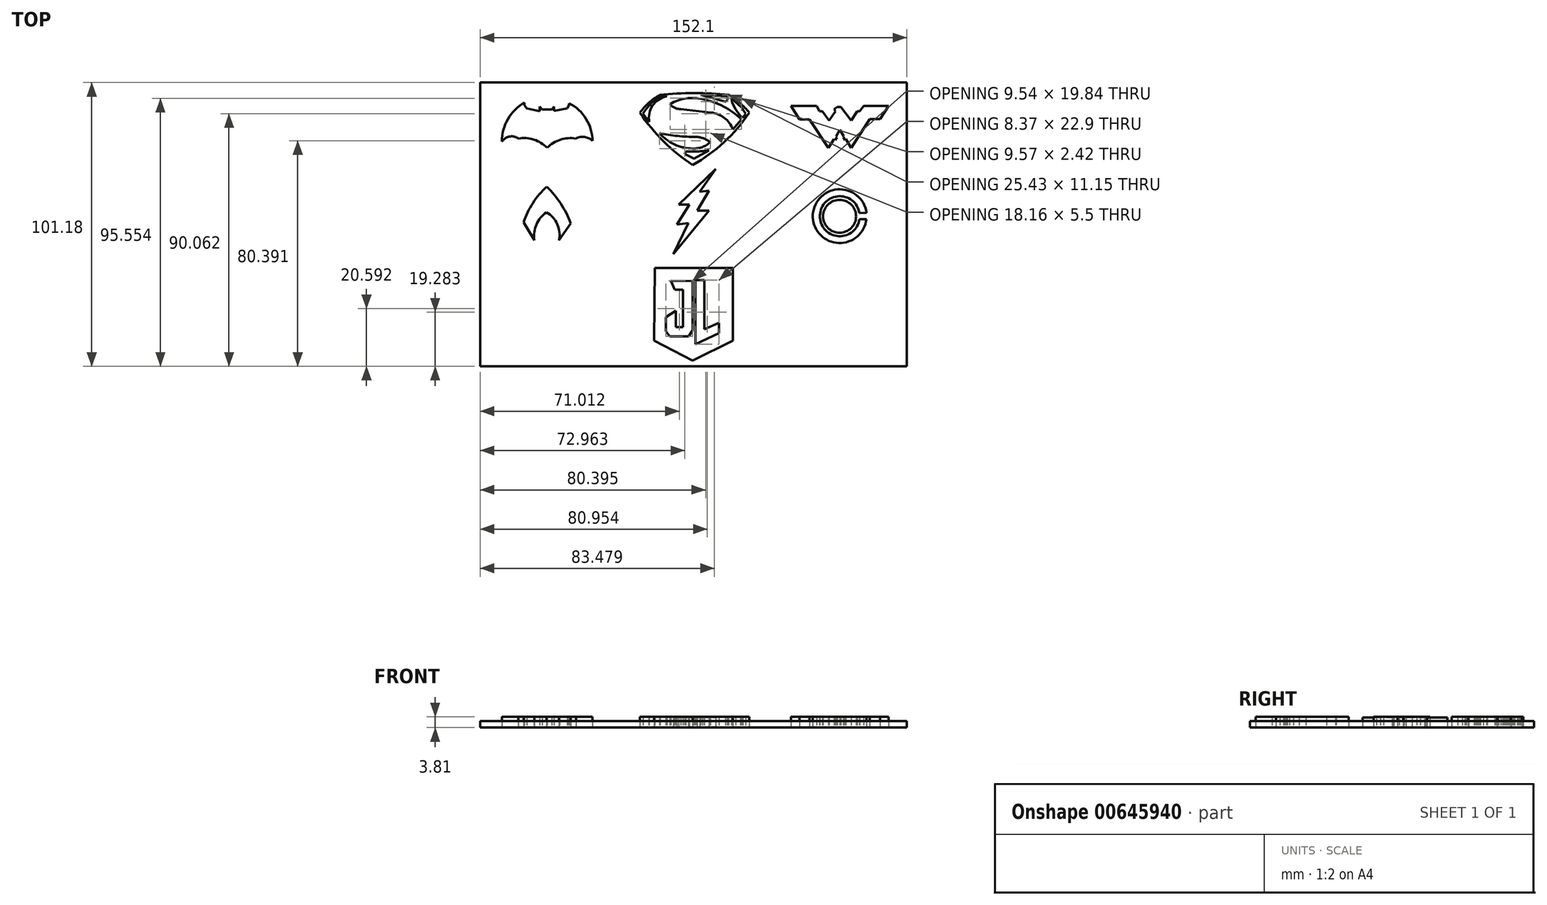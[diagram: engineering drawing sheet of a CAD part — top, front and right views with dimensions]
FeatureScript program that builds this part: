
annotation { "Feature Type Name" : "Feature", "Feature Type Description" : "" }
export const myFeature = defineFeature(function(context is Context, id is Id, definition is map)
    precondition{}
    {
        {
            var Q0;
            Q0=qCreatedBy(makeId("Top.planeOp"),FACE);
            var sketch = newSketch(context, id + "F0", { "sketchPlane" : qUnion([Q0])});
            skLineSegment(sketch, "E0.bottom", {"start": v(-75.78, 55.4) * mm, "end": v(76.32, 55.4) * mm});
            skLineSegment(sketch, "E0.top", {"start": v(-75.78, -45.78) * mm, "end": v(76.32, -45.78) * mm});
            skLineSegment(sketch, "E0.left", {"start": v(-75.78, 55.4) * mm, "end": v(-75.78, -45.78) * mm});
            skLineSegment(sketch, "E0.right", {"start": v(76.32, 55.4) * mm, "end": v(76.32, -45.78) * mm});
            skSolve(sketch);
        }
        {
            var Q0;
            Q0=makeQuery(id+"F0.imprint","IMPRINT",FACE,{"disambiguationData":[TD([[makeQuery(id+"F0.imprint","IMPRINT",EDGE,{"derivedFrom":sQuery(id+"F0.wireOp",EDGE,"E0.bottom")}),-1.0]])]});
            var sketch = newSketch(context, id + "F1", { "sketchPlane" : qUnion([Q0])});
            skLineSegment(sketch, "E1", {"start": v(-59.95, 48.2) * mm, "end": v(-59.95, 47.3) * mm});
            skLineSegment(sketch, "E2", {"start": v(-59.95, 47.3) * mm, "end": v(-59.08, 46.2) * mm});
            skLineSegment(sketch, "E3", {"start": v(-59.08, 46.2) * mm, "end": v(-54.48, 45.15) * mm});
            skLineSegment(sketch, "E4", {"start": v(-54.48, 45.15) * mm, "end": v(-54.48, 46.8) * mm});
            skLineSegment(sketch, "E5", {"start": v(-54.48, 46.8) * mm, "end": v(-53.64, 45.8) * mm});
            skLineSegment(sketch, "E6", {"start": v(-53.64, 45.8) * mm, "end": v(-50.18, 45.8) * mm});
            skLineSegment(sketch, "E7", {"start": v(-50.18, 45.8) * mm, "end": v(-49.45, 46.84) * mm});
            skLineSegment(sketch, "E8", {"start": v(-49.45, 46.84) * mm, "end": v(-49.45, 45.24) * mm});
            skLineSegment(sketch, "E9", {"start": v(-49.45, 45.24) * mm, "end": v(-44.72, 46.23) * mm});
            skLineSegment(sketch, "E10", {"start": v(-44.72, 46.23) * mm, "end": v(-44.22, 47.1) * mm});
            skLineSegment(sketch, "E11", {"start": v(-44.22, 47.1) * mm, "end": v(-43.96, 47.97) * mm});
            skArc(sketch, "E12", {"start": v(-35.7, 34.6) * mm, "mid": v(-38, 42.42) * mm, "end": v(-43.96, 47.97) * mm});
            skArc(sketch, "E13", {"start": v(-35.7, 34.6) * mm, "mid": v(-38.53, 35.98) * mm, "end": v(-41.63, 35.44) * mm});
            skArc(sketch, "E14", {"start": v(-41.63, 35.44) * mm, "mid": v(-47.16, 35.03) * mm, "end": v(-51.9, 32.16) * mm});
            skArc(sketch, "E15", {"start": v(-51.9, 32.16) * mm, "mid": v(-56.6, 35.05) * mm, "end": v(-62.1, 35.44) * mm});
            skArc(sketch, "E16", {"start": v(-62.1, 35.44) * mm, "mid": v(-65.25, 36.15) * mm, "end": v(-67.94, 34.35) * mm});
            skArc(sketch, "E17", {"start": v(-59.95, 48.2) * mm, "mid": v(-65.88, 42.39) * mm, "end": v(-67.94, 34.35) * mm});
            skSolve(sketch);
        }
        {
            var Q0;
            Q0=qCreatedBy(makeId("Top.planeOp"),FACE);
            var sketch = newSketch(context, id + "F2", { "sketchPlane" : qUnion([Q0])});
            skArc(sketch, "E18", {"start": v(-52.01, 18.27) * mm, "mid": v(-56.96, 12.44) * mm, "end": v(-60.24, 5.53) * mm});
            skLineSegment(sketch, "E19", {"start": v(-60.24, 5.53) * mm, "end": v(-56.46, -0.8) * mm});
            skArc(sketch, "E20", {"start": v(-52.1, 9.15) * mm, "mid": v(-55.72, 4.8) * mm, "end": v(-56.46, -0.8) * mm});
            skArc(sketch, "E21", {"start": v(-47.66, -0.8) * mm, "mid": v(-48.28, 4.89) * mm, "end": v(-52.1, 9.15) * mm});
            skLineSegment(sketch, "E22", {"start": v(-47.66, -0.8) * mm, "end": v(-43.46, 5.2) * mm});
            skArc(sketch, "E23", {"start": v(-43.46, 5.2) * mm, "mid": v(-47, 12.21) * mm, "end": v(-52.01, 18.27) * mm});
            skSolve(sketch);
        }
        {
            var Q0;
            Q0=qCreatedBy(makeId("Top.planeOp"),FACE);
            var sketch = newSketch(context, id + "F3", { "sketchPlane" : qUnion([Q0])});
            skLineSegment(sketch, "E24", {"start": v(8.22, 24.54) * mm, "end": v(-4.99, 11.94) * mm});
            skLineSegment(sketch, "E25", {"start": v(-4.99, 11.94) * mm, "end": v(-1.2, 11.94) * mm});
            skLineSegment(sketch, "E26", {"start": v(-1.2, 11.94) * mm, "end": v(-5.65, 4.83) * mm});
            skLineSegment(sketch, "E27", {"start": v(-5.65, 4.83) * mm, "end": v(-1.62, 5.32) * mm});
            skLineSegment(sketch, "E28", {"start": v(-1.62, 5.32) * mm, "end": v(-6.88, -5.74) * mm});
            skLineSegment(sketch, "E29", {"start": v(-6.88, -5.74) * mm, "end": v(5.8, 9.8) * mm});
            skLineSegment(sketch, "E30", {"start": v(5.8, 9.8) * mm, "end": v(1.67, 9.8) * mm});
            skLineSegment(sketch, "E31", {"start": v(1.67, 9.8) * mm, "end": v(5.86, 16.8) * mm});
            skLineSegment(sketch, "E32", {"start": v(5.86, 16.8) * mm, "end": v(2.49, 16.45) * mm});
            skLineSegment(sketch, "E33", {"start": v(2.49, 16.45) * mm, "end": v(8.22, 24.54) * mm});
            skSolve(sketch);
        }
        {
            var Q0;
            Q0=qCreatedBy(makeId("Top.planeOp"),FACE);
            var sketch = newSketch(context, id + "F4", { "sketchPlane" : qUnion([Q0])});
            skCircle(sketch, "E34", {"center": v(52.34, 7.72) * mm, "radius": 5.87 * mm});
            skArc(sketch, "E35", {"start": v(61.92, 8.95) * mm, "mid": v(51.6, 17.3) * mm, "end": v(42.8, 7.35) * mm});
            skArc(sketch, "E36", {"start": v(42.8, 7.35) * mm, "mid": v(52.04, -1.8) * mm, "end": v(61.88, 6.69) * mm});
            skLineSegment(sketch, "E37", {"start": v(61.88, 6.69) * mm, "end": v(59.42, 6.69) * mm});
            skArc(sketch, "E38", {"start": v(45.35, 7.35) * mm, "mid": v(52.09, 0.62) * mm, "end": v(59.42, 6.69) * mm});
            skArc(sketch, "E39", {"start": v(59.38, 8.83) * mm, "mid": v(51.65, 14.85) * mm, "end": v(45.35, 7.35) * mm});
            skLineSegment(sketch, "E40", {"start": v(59.38, 8.83) * mm, "end": v(61.92, 8.95) * mm});
            skSolve(sketch);
        }
        {
            var Q0;
            Q0=qCreatedBy(makeId("Top.planeOp"),FACE);
            var sketch = newSketch(context, id + "F5", { "sketchPlane" : qUnion([Q0])});
            skLineSegment(sketch, "E41", {"start": v(34.98, 47.06) * mm, "end": v(44.11, 47.06) * mm});
            skLineSegment(sketch, "E42", {"start": v(44.11, 47.06) * mm, "end": v(45.16, 45.14) * mm});
            skLineSegment(sketch, "E43", {"start": v(45.16, 45.14) * mm, "end": v(46.2, 45.14) * mm});
            skLineSegment(sketch, "E44", {"start": v(46.2, 45.14) * mm, "end": v(48.6, 41.88) * mm});
            skLineSegment(sketch, "E45", {"start": v(48.6, 41.88) * mm, "end": v(50.92, 45.14) * mm});
            skLineSegment(sketch, "E46", {"start": v(50.92, 45.14) * mm, "end": v(50.4, 45.91) * mm});
            skLineSegment(sketch, "E47", {"start": v(50.4, 45.91) * mm, "end": v(51.51, 46.66) * mm});
            skLineSegment(sketch, "E48", {"start": v(51.51, 46.66) * mm, "end": v(52.85, 46.66) * mm});
            skLineSegment(sketch, "E49", {"start": v(52.85, 46.66) * mm, "end": v(56.41, 41.86) * mm});
            skLineSegment(sketch, "E50", {"start": v(56.41, 41.86) * mm, "end": v(58.66, 45.14) * mm});
            skLineSegment(sketch, "E51", {"start": v(58.66, 45.14) * mm, "end": v(59.56, 45.14) * mm});
            skLineSegment(sketch, "E52", {"start": v(59.56, 45.14) * mm, "end": v(60.9, 47.09) * mm});
            skLineSegment(sketch, "E53", {"start": v(60.9, 47.09) * mm, "end": v(69.8, 47.09) * mm});
            skLineSegment(sketch, "E54", {"start": v(69.8, 47.09) * mm, "end": v(66.82, 42.31) * mm});
            skLineSegment(sketch, "E55", {"start": v(66.82, 42.31) * mm, "end": v(63.12, 42.31) * mm});
            skLineSegment(sketch, "E56", {"start": v(63.12, 42.31) * mm, "end": v(56.45, 32.05) * mm});
            skLineSegment(sketch, "E57", {"start": v(56.45, 32.05) * mm, "end": v(54.58, 35.26) * mm});
            skLineSegment(sketch, "E58", {"start": v(54.58, 35.26) * mm, "end": v(54.3, 34.83) * mm});
            skLineSegment(sketch, "E59", {"start": v(54.3, 34.83) * mm, "end": v(53.62, 35.9) * mm});
            skLineSegment(sketch, "E60", {"start": v(53.62, 35.9) * mm, "end": v(53.81, 36.3) * mm});
            skLineSegment(sketch, "E61", {"start": v(53.81, 36.3) * mm, "end": v(52.44, 38.55) * mm});
            skLineSegment(sketch, "E62", {"start": v(52.44, 38.55) * mm, "end": v(51.1, 36.32) * mm});
            skLineSegment(sketch, "E63", {"start": v(51.1, 36.32) * mm, "end": v(51.34, 35.88) * mm});
            skLineSegment(sketch, "E64", {"start": v(51.34, 35.88) * mm, "end": v(50.7, 34.88) * mm});
            skLineSegment(sketch, "E65", {"start": v(50.7, 34.88) * mm, "end": v(50.41, 35.26) * mm});
            skLineSegment(sketch, "E66", {"start": v(50.41, 35.26) * mm, "end": v(48.36, 32.05) * mm});
            skLineSegment(sketch, "E67", {"start": v(48.36, 32.05) * mm, "end": v(41.64, 42.25) * mm});
            skLineSegment(sketch, "E68", {"start": v(41.64, 42.25) * mm, "end": v(38.09, 42.25) * mm});
            skLineSegment(sketch, "E69", {"start": v(38.09, 42.25) * mm, "end": v(34.98, 47.06) * mm});
            skSolve(sketch);
        }
        {
            var Q0;
            Q0=qCreatedBy(makeId("Top.planeOp"),FACE);
            var sketch = newSketch(context, id + "F6", { "sketchPlane" : qUnion([Q0])});
            skArc(sketch, "E70", {"start": v(-11.68, 50.98) * mm, "mid": v(-15.6, 48.22) * mm, "end": v(-18.79, 44.64) * mm});
            skArc(sketch, "E71", {"start": v(-18.79, 44.64) * mm, "mid": v(-10.36, 34.37) * mm, "end": v(0, 26.04) * mm});
            skArc(sketch, "E72", {"start": v(0, 26.04) * mm, "mid": v(11.19, 34.14) * mm, "end": v(20.15, 44.64) * mm});
            skArc(sketch, "E73", {"start": v(20.15, 44.64) * mm, "mid": v(16.76, 48.18) * mm, "end": v(12.76, 51) * mm});
            skArc(sketch, "E74", {"start": v(12.76, 51) * mm, "mid": v(0.54, 51.62) * mm, "end": v(-11.68, 50.98) * mm});
            skLineSegment(sketch, "E75", {"start": v(17.87, 42.85) * mm, "end": v(18.86, 44.22) * mm});
            skLineSegment(sketch, "E76", {"start": v(18.86, 44.22) * mm, "end": v(17.3, 46.54) * mm});
            skLineSegment(sketch, "E77", {"start": v(17.3, 46.54) * mm, "end": v(13.83, 49.72) * mm});
            skLineSegment(sketch, "E78", {"start": v(13.83, 49.72) * mm, "end": v(14.07, 48.26) * mm});
            skLineSegment(sketch, "E79", {"start": v(14.07, 48.26) * mm, "end": v(15.32, 45.81) * mm});
            skLineSegment(sketch, "E80", {"start": v(15.32, 45.81) * mm, "end": v(17.03, 43.51) * mm});
            skLineSegment(sketch, "E81", {"start": v(17.03, 43.51) * mm, "end": v(17.87, 42.85) * mm});
            skLineSegment(sketch, "E82", {"start": v(2.92, 50.98) * mm, "end": v(12.25, 50.53) * mm});
            skArc(sketch, "E83", {"start": v(11.63, 48.56) * mm, "mid": v(12.43, 49.4) * mm, "end": v(12.25, 50.53) * mm});
            skLineSegment(sketch, "E84", {"start": v(11.63, 48.56) * mm, "end": v(2.92, 50.98) * mm});
            skLineSegment(sketch, "E85", {"start": v(-17.68, 44.33) * mm, "end": v(-15.47, 41.36) * mm});
            skArc(sketch, "E86", {"start": v(-9.17, 50.55) * mm, "mid": v(-14.24, 47.28) * mm, "end": v(-15.47, 41.36) * mm});
            skLineSegment(sketch, "E87", {"start": v(-9.17, 50.55) * mm, "end": v(-9.49, 50.5) * mm});
            skLineSegment(sketch, "E88", {"start": v(-11.61, 50.55) * mm, "end": v(-9.17, 50.55) * mm});
            skArc(sketch, "E89", {"start": v(-11.61, 50.55) * mm, "mid": v(-14.98, 47.77) * mm, "end": v(-17.68, 44.33) * mm});
            skLineSegment(sketch, "E90", {"start": v(-2.43, 30.78) * mm, "end": v(-2.82, 29.88) * mm});
            skLineSegment(sketch, "E91", {"start": v(-2.82, 29.88) * mm, "end": v(0.45, 28.24) * mm});
            skLineSegment(sketch, "E92", {"start": v(0.45, 28.24) * mm, "end": v(5.83, 31.2) * mm});
            skArc(sketch, "E93", {"start": v(-2.43, 30.78) * mm, "mid": v(1.7, 30.83) * mm, "end": v(5.83, 31.2) * mm});
            skArc(sketch, "E94", {"start": v(-11.9, 37.36) * mm, "mid": v(-6.53, 33.37) * mm, "end": v(0, 31.86) * mm});
            skArc(sketch, "E95", {"start": v(0, 31.86) * mm, "mid": v(3.35, 32.39) * mm, "end": v(6.27, 34.1) * mm});
            skArc(sketch, "E96", {"start": v(6.27, 34.1) * mm, "mid": v(3.89, 35.46) * mm, "end": v(1.2, 36.02) * mm});
            skArc(sketch, "E97", {"start": v(-11.9, 37.36) * mm, "mid": v(-5.38, 36.34) * mm, "end": v(1.2, 36.02) * mm});
            skLineSegment(sketch, "E98", {"start": v(14.35, 38.7) * mm, "end": v(17.33, 42.27) * mm});
            skArc(sketch, "E99", {"start": v(17.33, 42.27) * mm, "mid": v(10.95, 46.85) * mm, "end": v(3.54, 49.43) * mm});
            skArc(sketch, "E100", {"start": v(3.54, 49.43) * mm, "mid": v(-2.44, 49.72) * mm, "end": v(-8.1, 47.77) * mm});
            skArc(sketch, "E101", {"start": v(-8.1, 47.77) * mm, "mid": v(-6.43, 46.38) * mm, "end": v(-4.29, 45.96) * mm});
            skLineSegment(sketch, "E102", {"start": v(-4.29, 45.96) * mm, "end": v(6.57, 44.7) * mm});
            skArc(sketch, "E103", {"start": v(14.35, 38.7) * mm, "mid": v(11.28, 42.77) * mm, "end": v(6.57, 44.7) * mm});
            skSolve(sketch);
        }
        {
            var Q0;
            Q0=qCreatedBy(makeId("Top.planeOp"),FACE);
            var sketch = newSketch(context, id + "F7", { "sketchPlane" : qUnion([Q0])});
            skLineSegment(sketch, "E104", {"start": v(-13.55, -10.71) * mm, "end": v(14.25, -10.71) * mm});
            skLineSegment(sketch, "E105", {"start": v(14.25, -10.71) * mm, "end": v(14.25, -36.57) * mm});
            skLineSegment(sketch, "E106", {"start": v(14.25, -36.57) * mm, "end": v(0, -43.77) * mm});
            skLineSegment(sketch, "E107", {"start": v(0, -43.77) * mm, "end": v(-13.73, -36.58) * mm});
            skLineSegment(sketch, "E108", {"start": v(-13.73, -36.58) * mm, "end": v(-13.55, -10.71) * mm});
            skLineSegment(sketch, "E109", {"start": v(-7.74, -15.27) * mm, "end": v(-6.42, -18.52) * mm});
            skLineSegment(sketch, "E110", {"start": v(-6.42, -18.52) * mm, "end": v(-3.45, -18.52) * mm});
            skLineSegment(sketch, "E111", {"start": v(-3.45, -18.52) * mm, "end": v(-3.45, -31.8) * mm});
            skLineSegment(sketch, "E112", {"start": v(-3.45, -31.8) * mm, "end": v(-6, -31.8) * mm});
            skLineSegment(sketch, "E113", {"start": v(-6, -31.8) * mm, "end": v(-6, -25.91) * mm});
            skLineSegment(sketch, "E114", {"start": v(-6, -25.91) * mm, "end": v(-9.54, -28.27) * mm});
            skLineSegment(sketch, "E115", {"start": v(-9.54, -28.27) * mm, "end": v(-9.54, -33.38) * mm});
            skLineSegment(sketch, "E116", {"start": v(-9.54, -33.38) * mm, "end": v(-8.13, -35.11) * mm});
            skLineSegment(sketch, "E117", {"start": v(-8.13, -35.11) * mm, "end": v(-1.48, -35.11) * mm});
            skLineSegment(sketch, "E118", {"start": v(-1.48, -35.11) * mm, "end": v(0, -32.96) * mm});
            skLineSegment(sketch, "E119", {"start": v(0, -32.96) * mm, "end": v(0, -15.36) * mm});
            skLineSegment(sketch, "E120", {"start": v(0, -15.36) * mm, "end": v(-7.74, -15.27) * mm});
            skLineSegment(sketch, "E121", {"start": v(1, -15.04) * mm, "end": v(4.1, -15.04) * mm});
            skLineSegment(sketch, "E122", {"start": v(4.1, -15.04) * mm, "end": v(4.1, -32.54) * mm});
            skLineSegment(sketch, "E123", {"start": v(4.1, -32.54) * mm, "end": v(9.36, -30.33) * mm});
            skLineSegment(sketch, "E124", {"start": v(9.36, -30.33) * mm, "end": v(9.36, -33.91) * mm});
            skLineSegment(sketch, "E125", {"start": v(9.36, -33.91) * mm, "end": v(0.99, -37.95) * mm});
            skLineSegment(sketch, "E126", {"start": v(0.99, -37.95) * mm, "end": v(1, -15.04) * mm});
            skSolve(sketch);
        }
        {
            var Q0;
            Q0 = qSketchRegion(id + "F1", true);
            var Q1;
            Q1 = qSketchRegion(id + "F2", true);
            var Q2;
            Q2 = qSketchRegion(id + "F4", true);
            var Q3;
            Q3 = qSketchRegion(id + "F5", true);
            var Q4;
            Q4 = qSketchRegion(id + "F6", true);
            var Q5;
            Q5 = qSketchRegion(id + "F7", true);
            extrude(context, id + "F8", {"entities" : qUnion([Q0, Q1, Q2, Q3, Q4, Q5]), "depth" : 3.8 * mm, "offsetDistance" : 25.4 * mm});
        }
        {
            var Q0;
            Q0 = qSketchRegion(id + "F3", true);
            extrude(context, id + "F9", {"entities" : qUnion([Q0]), "depth" : 3.56 * mm, "offsetDistance" : 25.4 * mm});
        }
        {
            var Q0;
            Q0 = qSketchRegion(id + "F0", true);
            extrude(context, id + "F10", {"entities" : qUnion([Q0]), "depth" : 2.3 * mm, "offsetDistance" : 25.4 * mm});
        }
    });
